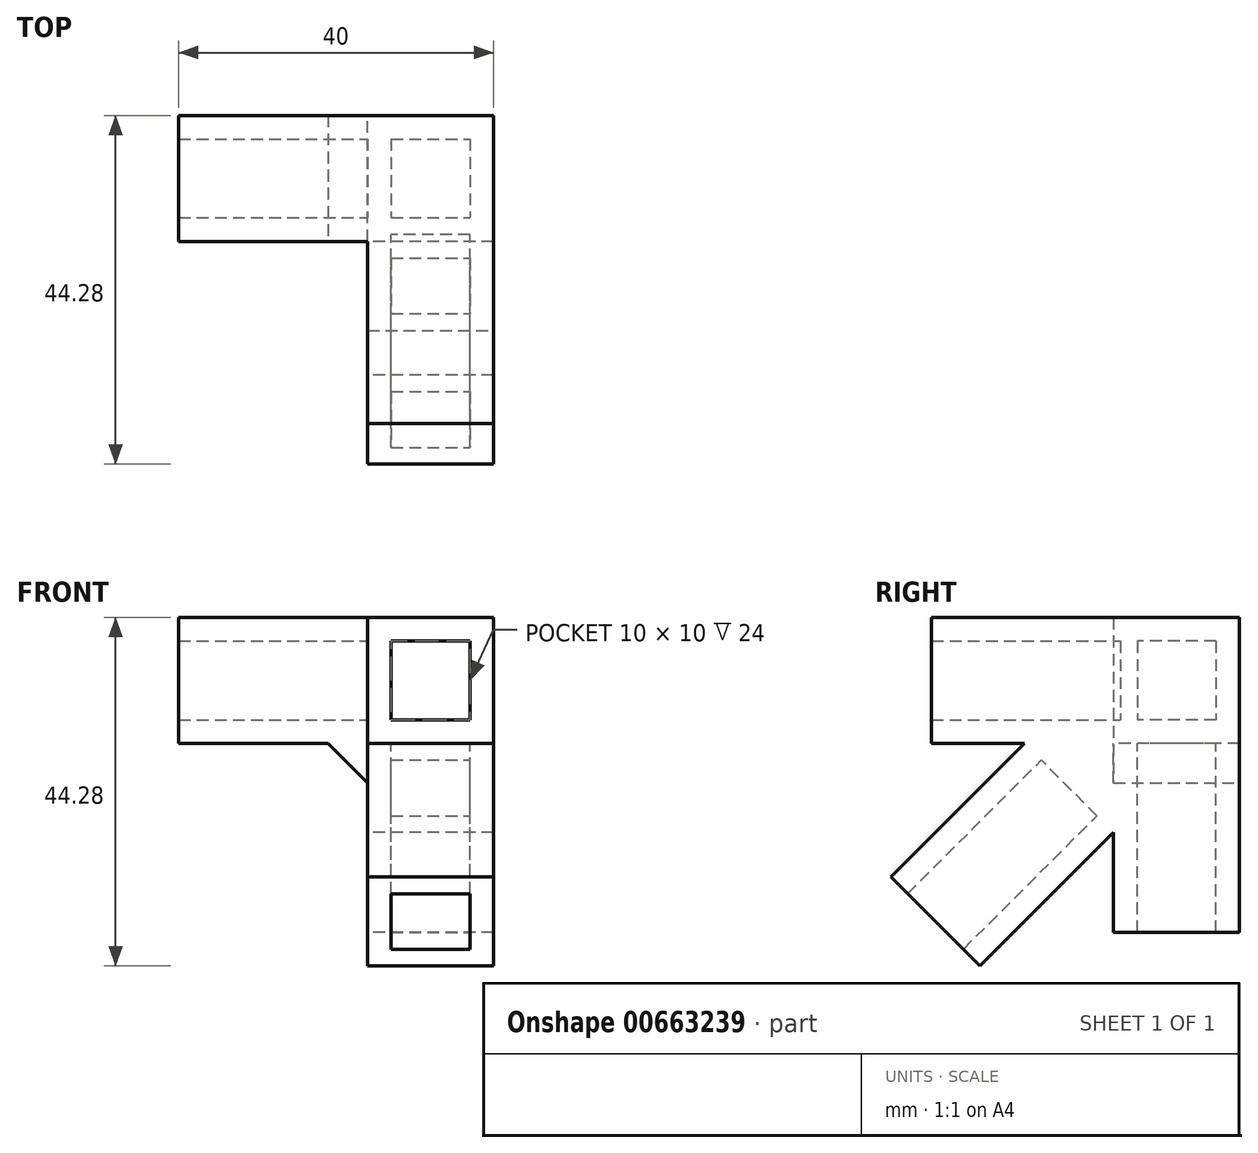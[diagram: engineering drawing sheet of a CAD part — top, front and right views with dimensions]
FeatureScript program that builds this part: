
annotation { "Feature Type Name" : "Feature", "Feature Type Description" : "" }
export const myFeature = defineFeature(function(context is Context, id is Id, definition is map)
    precondition{}
    {
        {
            var Q0;
            Q0=qCreatedBy(makeId("Front.planeOp"),FACE);
            var sketch = newSketch(context, id + "F0", { "sketchPlane" : qUnion([Q0])});
            skLineSegment(sketch, "E0.bottom", {"start": v(5, 5) * mm, "end": v(-5, 5) * mm});
            skLineSegment(sketch, "E0.top", {"start": v(5, -5) * mm, "end": v(-5, -5) * mm});
            skLineSegment(sketch, "E0.left", {"start": v(5, 5) * mm, "end": v(5, -5) * mm});
            skLineSegment(sketch, "E0.right", {"start": v(-5, 5) * mm, "end": v(-5, -5) * mm});
            skPoint(sketch, "E0.middle", {"position": v(0, 0) * mm});
            skLineSegment(sketch, "E1.0", {"start": v(8, 8) * mm, "end": v(-8, 8) * mm});
            skLineSegment(sketch, "E1.1", {"start": v(8, 8) * mm, "end": v(8, -8) * mm});
            skLineSegment(sketch, "E1.2", {"start": v(8, -8) * mm, "end": v(-8, -8) * mm});
            skLineSegment(sketch, "E1.3", {"start": v(-8, 8) * mm, "end": v(-8, -8) * mm});
            skSolve(sketch);
        }
        {
            var Q0;
            Q0=makeQuery(id+"F0.imprint","IMPRINT",FACE,{"disambiguationData":[TD([[makeQuery(id+"F0.imprint","IMPRINT",EDGE,{"derivedFrom":sQuery(id+"F0.wireOp",EDGE,"E0.bottom")}),-1.0]])]});
            extrude(context, id + "F1", {"entities" : qUnion([Q0]), "depth" : 32 * mm, "offsetDistance" : 25 * mm});
        }
        {
            var Q0;
            Q0=makeQuery(id+"F1.opExtrude","SWEPT_FACE",FACE,{"disambiguationData":[OSD([sQuery(id+"F0.wireOp",EDGE,"E1.0")])]});
            var sketch = newSketch(context, id + "F2", { "sketchPlane" : qUnion([Q0])});
            skLineSegment(sketch, "E2.bottom", {"start": v(8, -7.12) * mm, "end": v(-8, -7.12) * mm});
            skLineSegment(sketch, "E2.top", {"start": v(8, 7.12) * mm, "end": v(-8, 7.12) * mm});
            skLineSegment(sketch, "E2.left", {"start": v(8, -7.12) * mm, "end": v(8, 7.12) * mm});
            skLineSegment(sketch, "E2.right", {"start": v(-8, 0) * mm, "end": v(-8, 7.12) * mm});
            skPoint(sketch, "E2.middle", {"position": v(0, 0) * mm});
            skLineSegment(sketch, "E3", {"start": v(8, 0) * mm, "end": v(-8, 0) * mm});
            skSolve(sketch);
        }
        {
            var Q0;
            Q0 = qSketchRegion(id + "F2", true);
            var Q1;
            Q1=makeQuery(id+"F1.opExtrude","SWEPT_FACE",FACE,{"disambiguationData":[OSD([sQuery(id+"F0.wireOp",EDGE,"E1.2")])]});
            extrude(context, id + "F3", {"entities" : qUnion([Q0]), "operationType" : NewBodyOperationType.ADD, "endBound" : BoundingType.UP_TO_SURFACE, "oppositeDirection" : true, "depth" : 25 * mm, "endBoundEntityFace" : qUnion([Q1]), "offsetDistance" : 25 * mm});
        }
        {
            var Q0;
            {var subQ0=sQuery(id+"F0.wireOp",EDGE,"E1.2");Q0=makeQuery(id+"F3.boolean.opBoolean","MERGE",FACE,{"derivedFrom":[makeQuery(id+"F1.opExtrude","SWEPT_FACE",FACE,{"disambiguationData":[OSD([subQ0])]}),makeQuery(id+"F3.opExtrude","CAP_FACE",FACE,{"disambiguationData":[OSD([subQ0])],"isStart":false})]});}
            var sketch = newSketch(context, id + "F4", { "sketchPlane" : qUnion([Q0])});
            skLineSegment(sketch, "E4.bottom", {"start": v(-8, -7.12) * mm, "end": v(8, -7.12) * mm});
            skLineSegment(sketch, "E4.top", {"start": v(-8, 8.88) * mm, "end": v(8, 8.88) * mm});
            skLineSegment(sketch, "E4.left", {"start": v(-8, -7.12) * mm, "end": v(-8, 8.88) * mm});
            skLineSegment(sketch, "E4.right", {"start": v(8, -7.12) * mm, "end": v(8, 8.88) * mm});
            skLineSegment(sketch, "E5.0", {"start": v(-5, 5.88) * mm, "end": v(5, 5.88) * mm});
            skLineSegment(sketch, "E5.1", {"start": v(-5, -4.12) * mm, "end": v(-5, 5.88) * mm});
            skLineSegment(sketch, "E5.2", {"start": v(-5, -4.12) * mm, "end": v(5, -4.12) * mm});
            skLineSegment(sketch, "E5.3", {"start": v(5, -4.12) * mm, "end": v(5, 5.88) * mm});
            skSolve(sketch);
        }
        {
            var Q0;
            Q0 = qSketchRegion(id + "F4", true);
            extrude(context, id + "F5", {"entities" : qUnion([Q0]), "operationType" : NewBodyOperationType.ADD, "depth" : 24 * mm, "offsetDistance" : 25 * mm});
        }
        {
            var Q0;
            Q0=makeQuery(id+"F5.boolean.opBoolean","MERGE",FACE,{"derivedFrom":[makeQuery(id+"F3.boolean.opBoolean","MERGE",FACE,{"derivedFrom":[makeQuery(id+"F1.opExtrude","SWEPT_FACE",FACE,{"disambiguationData":[OSD([sQuery(id+"F0.wireOp",EDGE,"E1.3")])]}),makeQuery(id+"F3.opExtrude","SWEPT_FACE",FACE,{"disambiguationData":[OSD([sQuery(id+"F2.wireOp",EDGE,"E2.right")])]})]}),makeQuery(id+"F5.opExtrude","SWEPT_FACE",FACE,{"disambiguationData":[OSD([sQuery(id+"F4.wireOp",EDGE,"E4.left")])]})]});
            var sketch = newSketch(context, id + "F6", { "sketchPlane" : qUnion([Q0])});
            skLineSegment(sketch, "E6.bottom", {"start": v(-7.12, 8) * mm, "end": v(8.88, 8) * mm});
            skLineSegment(sketch, "E6.top", {"start": v(-7.12, -8) * mm, "end": v(8.88, -8) * mm});
            skLineSegment(sketch, "E6.left", {"start": v(-7.12, 8) * mm, "end": v(-7.12, -8) * mm});
            skLineSegment(sketch, "E6.right", {"start": v(8.88, 8) * mm, "end": v(8.88, -8) * mm});
            skLineSegment(sketch, "E7.0", {"start": v(5.88, 5) * mm, "end": v(5.88, -5) * mm});
            skLineSegment(sketch, "E7.1", {"start": v(-4.12, 5) * mm, "end": v(5.88, 5) * mm});
            skLineSegment(sketch, "E7.2", {"start": v(-4.12, 5) * mm, "end": v(-4.12, -5) * mm});
            skLineSegment(sketch, "E7.3", {"start": v(-4.12, -5) * mm, "end": v(5.88, -5) * mm});
            skSolve(sketch);
        }
        {
            var Q0;
            Q0=makeQuery(id+"F6.imprint","IMPRINT",FACE,{"disambiguationData":[TD([[makeQuery(id+"F6.imprint","IMPRINT",EDGE,{"derivedFrom":sQuery(id+"F6.wireOp",EDGE,"E6.bottom")}),1.0]])]});
            extrude(context, id + "F7", {"entities" : qUnion([Q0]), "operationType" : NewBodyOperationType.ADD, "depth" : 24 * mm, "offsetDistance" : 25 * mm});
        }
        {
            var Q0;
            Q0=makeQuery(id+"F5.opExtrude","CAP_EDGE",EDGE,{"disambiguationData":[OSD([sQuery(id+"F4.wireOp",EDGE,"E4.top")])],"isStart":true});
            chamfer(context, id + "F8", {"entities" : qUnion([Q0]), "width" : 11.3 * mm, "tangentPropagation" : true});
        }
        {
            var Q0;
            Q0=makeQuery(id+"F8.opChamfer","BLEND_FACE",FACE,{"disambiguationData":[OSD([sQuery(id+"F4.wireOp",EDGE,"E4.top")])]});
            var sketch = newSketch(context, id + "F9", { "sketchPlane" : qUnion([Q0])});
            skLineSegment(sketch, "E8.bottom", {"start": v(-8, -7.38) * mm, "end": v(8, -7.38) * mm});
            skLineSegment(sketch, "E8.top", {"start": v(-8, 8.62) * mm, "end": v(8, 8.62) * mm});
            skLineSegment(sketch, "E8.left", {"start": v(-8, -7.38) * mm, "end": v(-8, 8.62) * mm});
            skLineSegment(sketch, "E8.right", {"start": v(8, -7.38) * mm, "end": v(8, 8.62) * mm});
            skLineSegment(sketch, "E9.0", {"start": v(-5, -4.38) * mm, "end": v(-5, 5.62) * mm});
            skLineSegment(sketch, "E9.1", {"start": v(-5, -4.38) * mm, "end": v(5, -4.38) * mm});
            skLineSegment(sketch, "E9.2", {"start": v(5, -4.38) * mm, "end": v(5, 5.62) * mm});
            skLineSegment(sketch, "E9.3", {"start": v(-5, 5.62) * mm, "end": v(5, 5.62) * mm});
            skSolve(sketch);
        }
        {
            var Q0;
            Q0 = qSketchRegion(id + "F9", true);
            extrude(context, id + "F10", {"entities" : qUnion([Q0]), "operationType" : NewBodyOperationType.ADD, "depth" : 24 * mm, "offsetDistance" : 25 * mm});
        }
        {
            var Q0;
            Q0=makeQuery(id+"F7.opExtrude","CAP_EDGE",EDGE,{"disambiguationData":[OSD([sQuery(id+"F6.wireOp",EDGE,"E6.top")])],"isStart":true});
            var Q1;
            Q1=makeQuery(id+"F7.opExtrude","CAP_EDGE",EDGE,{"disambiguationData":[OSD([sQuery(id+"F6.wireOp",EDGE,"E6.right")])],"isStart":true});
            chamfer(context, id + "F11", {"entities" : qUnion([Q0, Q1]), "width" : 5 * mm, "tangentPropagation" : true});
        }
        {
            var Q0;
            Q0=makeQuery(id+"F3.opExtrude","SWEPT_FACE",FACE,{"disambiguationData":[OSD([sQuery(id+"F2.wireOp",EDGE,"E3")])]});
            var sketch = newSketch(context, id + "F12", { "sketchPlane" : qUnion([Q0])});
            skLineSegment(sketch, "E10.bottom", {"start": v(-5, -5) * mm, "end": v(5, -5) * mm});
            skLineSegment(sketch, "E10.top", {"start": v(-5, 5) * mm, "end": v(5, 5) * mm});
            skLineSegment(sketch, "E10.left", {"start": v(-5, -5) * mm, "end": v(-5, 5) * mm});
            skLineSegment(sketch, "E10.right", {"start": v(5, -5) * mm, "end": v(5, 5) * mm});
            skPoint(sketch, "E10.middle", {"position": v(0, 0) * mm});
            skSolve(sketch);
        }
        {
            var Q0;
            Q0=makeQuery(id+"F12.imprint","IMPRINT",FACE,{"disambiguationData":[TD([[makeQuery(id+"F12.imprint","IMPRINT",EDGE,{"derivedFrom":sQuery(id+"F12.wireOp",EDGE,"E10.bottom")}),-1.0]])]});
            extrude(context, id + "F13", {"entities" : qUnion([Q0]), "operationType" : NewBodyOperationType.ADD, "depth" : 8 * mm, "offsetDistance" : 25 * mm});
        }
    });
